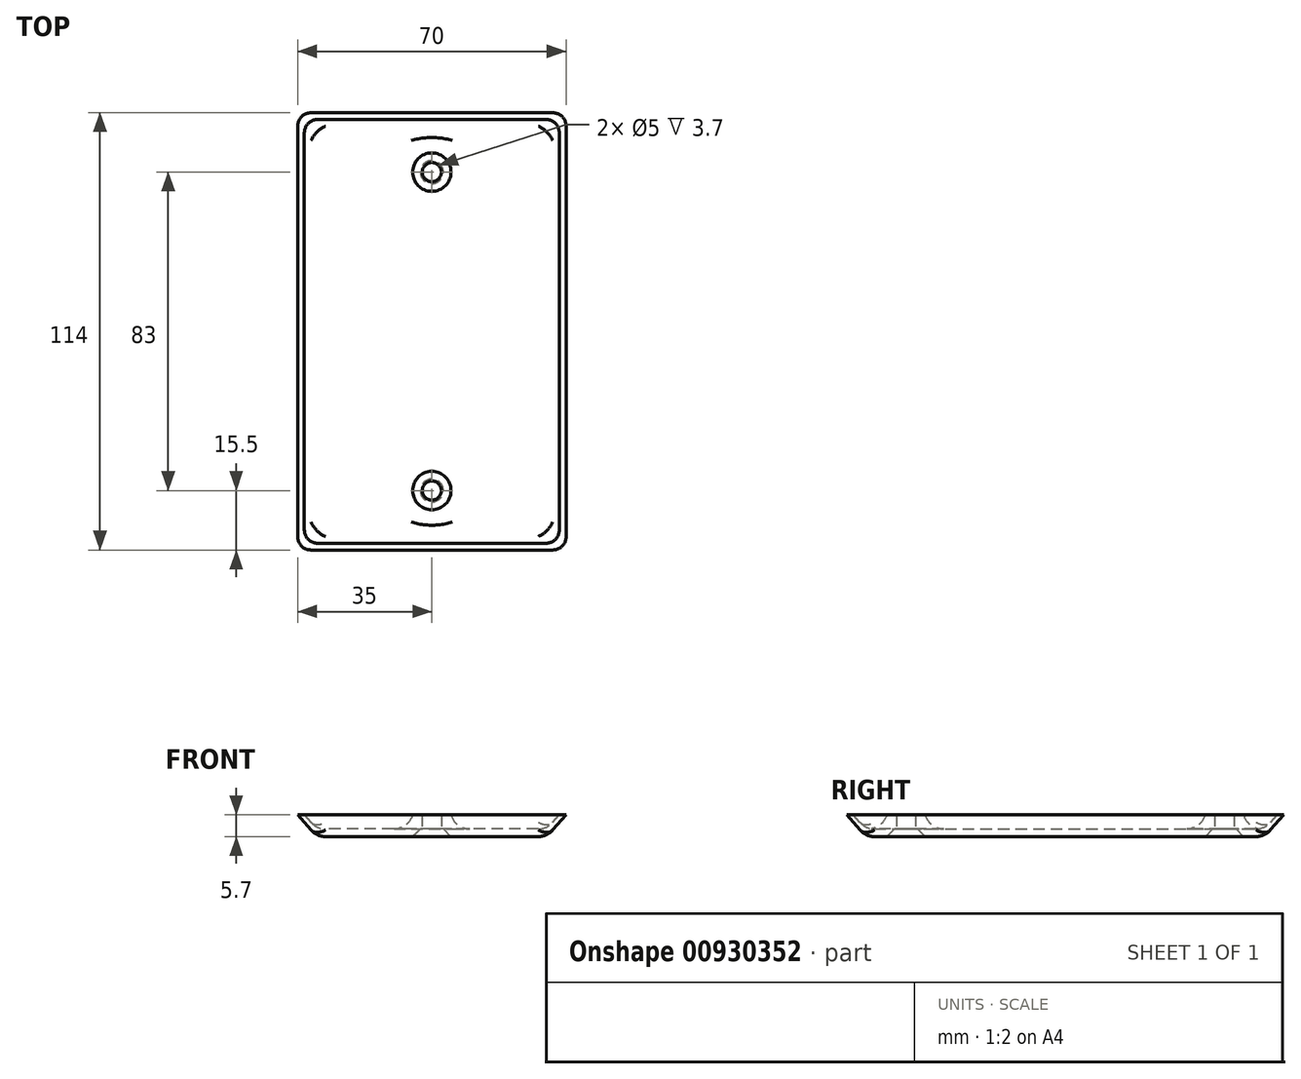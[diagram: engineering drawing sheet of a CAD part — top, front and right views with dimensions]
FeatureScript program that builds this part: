
annotation { "Feature Type Name" : "Feature", "Feature Type Description" : "" }
export const myFeature = defineFeature(function(context is Context, id is Id, definition is map)
    precondition{}
    {
        {
            var Q0;
            Q0=qCreatedBy(makeId("Top.planeOp"),FACE);
            var sketch = newSketch(context, id + "F0", { "sketchPlane" : qUnion([Q0])});
            skLineSegment(sketch, "E0.bottom", {"start": v(30, -52) * mm, "end": v(-30, -52) * mm});
            skLineSegment(sketch, "E0.top", {"start": v(30, 52) * mm, "end": v(-30, 52) * mm});
            skLineSegment(sketch, "E0.left", {"start": v(30, -52) * mm, "end": v(30, 52) * mm});
            skLineSegment(sketch, "E0.right", {"start": v(-30, -52) * mm, "end": v(-30, 52) * mm});
            skPoint(sketch, "E0.middle", {"position": v(0, 0) * mm});
            skSolve(sketch);
        }
        {
            var Q0;
            Q0=makeQuery(id+"F0.imprint","IMPRINT",FACE,{"disambiguationData":[TD([[makeQuery(id+"F0.imprint","IMPRINT",EDGE,{"derivedFrom":sQuery(id+"F0.wireOp",EDGE,"E0.bottom")}),-1.0]])]});
            cPlane(context, id + "F1", {"entities" : qUnion([Q0]), "cplaneType" : CPlaneType.OFFSET, "offset" : 5.7 * mm, "width" : 150 * mm, "height" : 150 * mm});
        }
        {
            var Q0;
            Q0=qCreatedBy(id+"F1.planeOp",FACE);
            var sketch = newSketch(context, id + "F2", { "sketchPlane" : qUnion([Q0])});
            skLineSegment(sketch, "E1.bottom", {"start": v(35, -57) * mm, "end": v(-35, -57) * mm});
            skLineSegment(sketch, "E1.top", {"start": v(35, 57) * mm, "end": v(-35, 57) * mm});
            skLineSegment(sketch, "E1.left", {"start": v(35, -57) * mm, "end": v(35, 57) * mm});
            skLineSegment(sketch, "E1.right", {"start": v(-35, -57) * mm, "end": v(-35, 57) * mm});
            skPoint(sketch, "E1.middle", {"position": v(0, 0) * mm});
            skSolve(sketch);
        }
        {
            var Q0;
            Q0 = qSketchRegion(id + "F0", true);
            var Q1;
            Q1 = qSketchRegion(id + "F2", true);
            loft(context, id + "F3", {"sheetProfilesArray" : [{ "sheetProfileEntities" : qUnion([Q0]) }, { "sheetProfileEntities" : qUnion([Q1]) }]});
        }
        {
            var Q0;
            Q0=makeQuery(id+"F3.opLoft","CAP_FACE",FACE,{"disambiguationData":[OSD([makeQuery(id+"F0.imprint","IMPRINT",FACE,{"disambiguationData":[TD([[makeQuery(id+"F0.imprint","IMPRINT",EDGE,{"derivedFrom":sQuery(id+"F0.wireOp",EDGE,"E0.bottom")}),-1.0]])]})])],"isStart":true});
            var sketch = newSketch(context, id + "F4", { "sketchPlane" : qUnion([Q0])});
            skLineSegment(sketch, "E2", {"start": v(0, 57) * mm, "end": v(0, 0) * mm, "construction": true});
            skLineSegment(sketch, "E3", {"start": v(0, 0) * mm, "end": v(0, -57) * mm, "construction": true});
            skPoint(sketch, "E4", {"position": v(0, 41.5) * mm});
            skPoint(sketch, "E5", {"position": v(0, -41.5) * mm});
            skSolve(sketch);
        }
        {
            var Q0;
            Q0=sQuery(id+"F4.wireOp",VERTEX,"E4");
            var Q1;
            Q1=sQuery(id+"F4.wireOp",VERTEX,"E5");
            var Q2;
            Q2=makeQuery(id+"F3.opLoft","SWEPT_BODY",BODY,{"disambiguationData":[OSD([makeQuery(id+"F0.imprint","IMPRINT",FACE,{"disambiguationData":[TD([[makeQuery(id+"F0.imprint","IMPRINT",EDGE,{"derivedFrom":sQuery(id+"F0.wireOp",EDGE,"E0.bottom")}),-1.0]])]}),makeQuery(id+"F2.imprint","IMPRINT",FACE,{"disambiguationData":[TD([[makeQuery(id+"F2.imprint","IMPRINT",EDGE,{"derivedFrom":sQuery(id+"F2.wireOp",EDGE,"E1.bottom")}),-1.0]])]})])]});
            hole(context, id + "F5", {"style" : HoleStyle.C_SINK, "endStyle" : HoleEndStyle.THROUGH, "holeDiameter" : 5 * mm, "cSinkDiameter" : 10 * mm, "cSinkAngle" : 90 * degree, "majorDiameter" : 5 * mm, "isTappedThrough" : true, "tappedDepth" : 12 * mm, "tapClearance" : 3, "locations" : qUnion([Q0, Q1]), "scope" : qUnion([Q2])});
        }
        {
            var Q0;
            Q0=makeQuery(id+"F3.opLoft","SWEPT_EDGE",EDGE,{"disambiguationData":[OSD([sQuery(id+"F0.wireOp",EDGE,"E0.bottom"),sQuery(id+"F0.wireOp",EDGE,"E0.left"),sQuery(id+"F2.wireOp",EDGE,"E1.bottom"),sQuery(id+"F2.wireOp",EDGE,"E1.left")])]});
            var Q1;
            Q1=makeQuery(id+"F3.opLoft","SWEPT_EDGE",EDGE,{"disambiguationData":[OSD([sQuery(id+"F0.wireOp",EDGE,"E0.bottom"),sQuery(id+"F0.wireOp",EDGE,"E0.right"),sQuery(id+"F2.wireOp",EDGE,"E1.bottom"),sQuery(id+"F2.wireOp",EDGE,"E1.right")])]});
            var Q2;
            Q2=makeQuery(id+"F3.opLoft","SWEPT_EDGE",EDGE,{"disambiguationData":[OSD([sQuery(id+"F0.wireOp",EDGE,"E0.top"),sQuery(id+"F0.wireOp",EDGE,"E0.right"),sQuery(id+"F2.wireOp",EDGE,"E1.top"),sQuery(id+"F2.wireOp",EDGE,"E1.right")])]});
            var Q3;
            Q3=makeQuery(id+"F3.opLoft","SWEPT_EDGE",EDGE,{"disambiguationData":[OSD([sQuery(id+"F0.wireOp",EDGE,"E0.top"),sQuery(id+"F0.wireOp",EDGE,"E0.left"),sQuery(id+"F2.wireOp",EDGE,"E1.top"),sQuery(id+"F2.wireOp",EDGE,"E1.left")])]});
            var Q4;
            Q4=makeQuery(id+"F3.opLoft","MID_CAP_EDGE",EDGE,{"disambiguationData":[OSD([sQuery(id+"F0.wireOp",EDGE,"E0.bottom"),sQuery(id+"F0.wireOp",EDGE,"E0.top"),sQuery(id+"F0.wireOp",EDGE,"E0.left")])],"capPos":0.0});
            var Q5;
            Q5=makeQuery(id+"F3.opLoft","MID_CAP_EDGE",EDGE,{"disambiguationData":[OSD([sQuery(id+"F0.wireOp",EDGE,"E0.top"),sQuery(id+"F0.wireOp",EDGE,"E0.left"),sQuery(id+"F0.wireOp",EDGE,"E0.right")])],"capPos":0.0});
            var Q6;
            Q6=makeQuery(id+"F3.opLoft","MID_CAP_EDGE",EDGE,{"disambiguationData":[OSD([sQuery(id+"F0.wireOp",EDGE,"E0.bottom"),sQuery(id+"F0.wireOp",EDGE,"E0.top"),sQuery(id+"F0.wireOp",EDGE,"E0.right")])],"capPos":0.0});
            var Q7;
            Q7=makeQuery(id+"F3.opLoft","MID_CAP_EDGE",EDGE,{"disambiguationData":[OSD([sQuery(id+"F0.wireOp",EDGE,"E0.bottom"),sQuery(id+"F0.wireOp",EDGE,"E0.left"),sQuery(id+"F0.wireOp",EDGE,"E0.right")])],"capPos":0.0});
            fillet(context, id + "F6", {"entities" : qUnion([Q0, Q1, Q2, Q3, Q4, Q5, Q6, Q7]), "radius" : 5 * mm, "tangentPropagation" : true, "allowEdgeOverflow" : false});
        }
        {
            var Q0;
            Q0=makeQuery(id+"F3.opLoft","SWEPT_BODY",BODY,{"disambiguationData":[OSD([makeQuery(id+"F0.imprint","IMPRINT",FACE,{"disambiguationData":[TD([[makeQuery(id+"F0.imprint","IMPRINT",EDGE,{"derivedFrom":sQuery(id+"F0.wireOp",EDGE,"E0.bottom")}),-1.0]])]}),makeQuery(id+"F2.imprint","IMPRINT",FACE,{"disambiguationData":[TD([[makeQuery(id+"F2.imprint","IMPRINT",EDGE,{"derivedFrom":sQuery(id+"F2.wireOp",EDGE,"E1.bottom")}),-1.0]])]})])]});
            transform(context, id + "F7", {"entities" : qUnion([Q0]), "transformType" : TransformType.TRANSLATION_3D, "dx" : 0 * mm, "dy" : 0 * mm, "dz" : 2 * mm, "makeCopy" : true});
        }
        {
            var Q0;
            Q0=makeQuery(id+"F7.opPattern","COPY",BODY,{"derivedFrom":makeQuery(id+"F3.opLoft","SWEPT_BODY",BODY,{"disambiguationData":[OSD([makeQuery(id+"F0.imprint","IMPRINT",FACE,{"disambiguationData":[TD([[makeQuery(id+"F0.imprint","IMPRINT",EDGE,{"derivedFrom":sQuery(id+"F0.wireOp",EDGE,"E0.bottom")}),-1.0]])]}),makeQuery(id+"F2.imprint","IMPRINT",FACE,{"disambiguationData":[TD([[makeQuery(id+"F2.imprint","IMPRINT",EDGE,{"derivedFrom":sQuery(id+"F2.wireOp",EDGE,"E1.bottom")}),-1.0]])]})])]}),"instanceName":"1"});
            var Q1;
            Q1=makeQuery(id+"F3.opLoft","SWEPT_BODY",BODY,{"disambiguationData":[OSD([makeQuery(id+"F0.imprint","IMPRINT",FACE,{"disambiguationData":[TD([[makeQuery(id+"F0.imprint","IMPRINT",EDGE,{"derivedFrom":sQuery(id+"F0.wireOp",EDGE,"E0.bottom")}),-1.0]])]}),makeQuery(id+"F2.imprint","IMPRINT",FACE,{"disambiguationData":[TD([[makeQuery(id+"F2.imprint","IMPRINT",EDGE,{"derivedFrom":sQuery(id+"F2.wireOp",EDGE,"E1.bottom")}),-1.0]])]})])]});
            booleanBodies(context, id + "F8", {"operationType" : BooleanOperationType.SUBTRACTION, "tools" : qUnion([Q0]), "targets" : qUnion([Q1])});
        }
        {
            var Q0;
            Q0=makeQuery(id+"F8.opBoolean","COPY",FACE,{"derivedFrom":makeQuery(id+"F7.opPattern","COPY",FACE,{"derivedFrom":makeQuery(id+"F3.opLoft","CAP_FACE",FACE,{"disambiguationData":[OSD([makeQuery(id+"F0.imprint","IMPRINT",FACE,{"disambiguationData":[TD([[makeQuery(id+"F0.imprint","IMPRINT",EDGE,{"derivedFrom":sQuery(id+"F0.wireOp",EDGE,"E0.bottom")}),-1.0]])]})])],"isStart":true}),"instanceName":"1"})});
            var sketch = newSketch(context, id + "F9", { "sketchPlane" : qUnion([Q0])});
            skCircle(sketch, "E6", {"center": v(0, 41.5) * mm, "radius": 5 * mm});
            skCircle(sketch, "E7", {"center": v(0, -41.5) * mm, "radius": 5 * mm});
            skCircle(sketch, "E8", {"center": v(0, 41.5) * mm, "radius": 2.5 * mm});
            skCircle(sketch, "E9", {"center": v(0, -41.5) * mm, "radius": 2.5 * mm});
            skSolve(sketch);
        }
        {
            var Q0;
            Q0 = qSketchRegion(id + "F9", true);
            var Q1;
            Q1=makeQuery(id+"F3.opLoft","CAP_FACE",FACE,{"disambiguationData":[OSD([makeQuery(id+"F2.imprint","IMPRINT",FACE,{"disambiguationData":[TD([[makeQuery(id+"F2.imprint","IMPRINT",EDGE,{"derivedFrom":sQuery(id+"F2.wireOp",EDGE,"E1.bottom")}),-1.0]])]})])],"isStart":true});
            extrude(context, id + "F10", {"entities" : qUnion([Q0]), "operationType" : NewBodyOperationType.ADD, "endBound" : BoundingType.UP_TO_SURFACE, "depth" : 2.5 * mm, "endBoundEntityFace" : qUnion([Q1]), "offsetDistance" : 25 * mm});
        }
        {
            var Q0;
            Q0=makeQuery(id+"F10.boolean.opBoolean","MERGE",EDGE,{"derivedFrom":[makeQuery(id+"F8.opBoolean","COPY",EDGE,{"derivedFrom":makeQuery(id+"F7.opPattern","COPY",EDGE,{"derivedFrom":makeQuery(id+"F5.hole-1.boolean.opBoolean","COPY",EDGE,{"derivedFrom":makeQuery(id+"F5.hole-1.opRevolve","SWEPT_EDGE",EDGE,{"disambiguationData":[OSD([sQuery(id+"F5.hole-1.sketch.wireOp",EDGE,"csink_start_line_1"),sQuery(id+"F5.hole-1.sketch.wireOp",EDGE,"csink_start_line_2")])]})}),"instanceName":"1"})}),makeQuery(id+"F10.opExtrude","CAP_EDGE",EDGE,{"disambiguationData":[OSD([sQuery(id+"F9.wireOp",EDGE,"E6")])],"isStart":true})]});
            var Q1;
            Q1=makeQuery(id+"F10.boolean.opBoolean","MERGE",EDGE,{"derivedFrom":[makeQuery(id+"F8.opBoolean","COPY",EDGE,{"derivedFrom":makeQuery(id+"F7.opPattern","COPY",EDGE,{"derivedFrom":makeQuery(id+"F5.hole-0.boolean.opBoolean","COPY",EDGE,{"derivedFrom":makeQuery(id+"F5.hole-0.opRevolve","SWEPT_EDGE",EDGE,{"disambiguationData":[OSD([sQuery(id+"F5.hole-0.sketch.wireOp",EDGE,"csink_start_line_1"),sQuery(id+"F5.hole-0.sketch.wireOp",EDGE,"csink_start_line_2")])]})}),"instanceName":"1"})}),makeQuery(id+"F10.opExtrude","CAP_EDGE",EDGE,{"disambiguationData":[OSD([sQuery(id+"F9.wireOp",EDGE,"E7")])],"isStart":true})]});
            fillet(context, id + "F11", {"entities" : qUnion([Q0, Q1]), "radius" : 5 * mm, "tangentPropagation" : true, "allowEdgeOverflow" : false});
        }
    });
